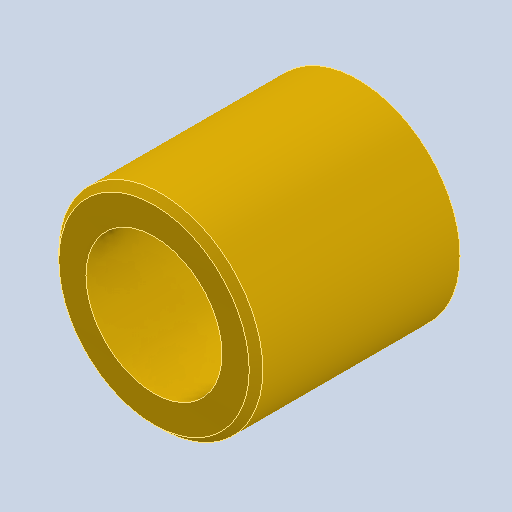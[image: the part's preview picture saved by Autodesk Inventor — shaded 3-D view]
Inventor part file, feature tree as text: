
AUTODESK INVENTOR PART (.ipt)
format: ipt  version: 2022 (Build 260153000, 153)  size: 111,104 bytes
history: native  units: in
note: dims shown in document units (in); Inventor stores cm internally (conversion verified against a paired STEP export)
features: extrude x1, chamfer x1, sketch x1
ambient origin geometry x8: Origin, YZ Plane, XZ Plane, XY Plane, X Axis, Y Axis, Z Axis, Center Point
bodies: Solid1 (feature_tree)
feature tree (3):
  extrude  "Extrusion1"  Depth=1.1811in
  chamfer  "Chamfer1"  Distance=1.1811in
  sketch  "Sketch1"  dims[d0=1.1811in d1=0.7874in d2=1.1811in d3=0.0in d4=0.0394in d5=0.0787in d6=45.0deg]
